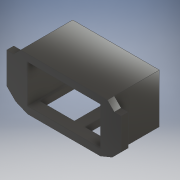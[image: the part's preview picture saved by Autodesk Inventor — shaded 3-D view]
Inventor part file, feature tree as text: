
AUTODESK INVENTOR PART (.ipt)
format: ipt  version: 2018 (Build 220112000, 112)  size: 316,928 bytes
history: native  units: mm
features: extrude x3, sketch x3, chamfer x2, shell x1, projected_geometry x1
ambient origin geometry x8: Origin, YZ Plane, XZ Plane, XY Plane, X Axis, Y Axis, Z Axis, Center Point
bodies: 实体1 (feature_tree)
feature tree (10):
  extrude  "拉伸1"  Depth=15.0mm
  shell  "抽壳1"  Thickness=25.0mm
  extrude  "拉伸2"  Depth=7.0mm
  extrude  "拉伸3"  Depth=3.0mm
  chamfer  "倒角1"  Distance=2.5mm
  chamfer  "倒角2"  Distance=5.0mm
  sketch  "草图1"  dims[d0=15.0mm d1=0.0mm d2=15.0mm d3=25.0mm]
  sketch  "草图2"  dims[d4=2.0mm d5=7.0mm]
  sketch  "草图3"  dims[d6=4.5mm d7=3.0mm d8=2.5mm d9=5.0mm d10=0.0mm d11=10.0mm d12=10.0mm d13=3.0mm d14=2.5mm d15=4.0mm d16=11.0mm d17=2.0mm d18=0.0mm d19=2.0mm d20=2.0mm d21=45.0deg d22=2.0mm d23=2.0mm d24=45.0deg]
  projected_geometry  "投影回路1"
